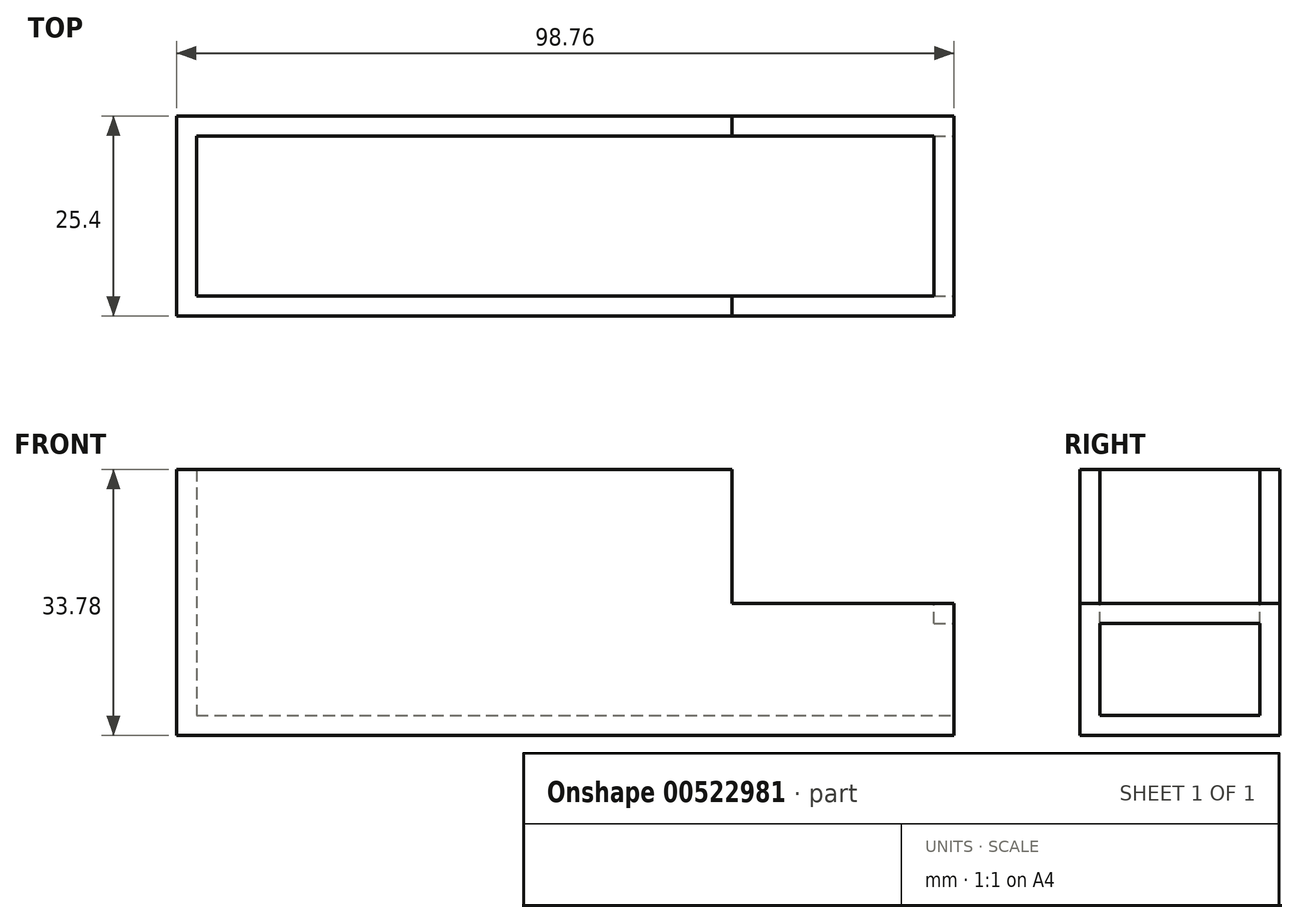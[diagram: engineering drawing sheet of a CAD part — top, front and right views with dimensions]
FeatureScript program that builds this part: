
annotation { "Feature Type Name" : "Feature", "Feature Type Description" : "" }
export const myFeature = defineFeature(function(context is Context, id is Id, definition is map)
    precondition{}
    {
        {
            var Q0;
            Q0=qCreatedBy(makeId("Front.planeOp"),FACE);
            var sketch = newSketch(context, id + "F0", { "sketchPlane" : qUnion([Q0])});
            skLineSegment(sketch, "E0.bottom", {"start": v(-70.56, 33.78) * mm, "end": v(0, 33.78) * mm});
            skLineSegment(sketch, "E0.top", {"start": v(-70.56, 0) * mm, "end": v(0, 0) * mm});
            skLineSegment(sketch, "E0.left", {"start": v(-70.56, 33.78) * mm, "end": v(-70.56, 0) * mm});
            skLineSegment(sketch, "E0.right", {"start": v(0, 33.78) * mm, "end": v(0, 0) * mm});
            skLineSegment(sketch, "E1.bottom", {"start": v(0, 0) * mm, "end": v(28.2, 0) * mm});
            skLineSegment(sketch, "E1.top", {"start": v(0, 16.76) * mm, "end": v(28.2, 16.76) * mm});
            skLineSegment(sketch, "E1.left", {"start": v(0, 0) * mm, "end": v(0, 16.76) * mm});
            skLineSegment(sketch, "E1.right", {"start": v(28.2, 0) * mm, "end": v(28.2, 16.76) * mm});
            skSolve(sketch);
        }
        {
            var Q0;
            Q0 = qSketchRegion(id + "F0", true);
            extrude(context, id + "F1", {"entities" : qUnion([Q0]), "depth" : 25.4 * mm, "offsetDistance" : 25.4 * mm});
        }
        {
            var Q0;
            Q0=makeQuery(id+"F1.opExtrude","SWEPT_FACE",FACE,{"disambiguationData":[OSD([sQuery(id+"F0.wireOp",EDGE,"E0.bottom")])]});
            var sketch = newSketch(context, id + "F2", { "sketchPlane" : qUnion([Q0])});
            skSolve(sketch);
        }
        {
            var Q0;
            Q0=makeQuery(id+"F1.opExtrude","CAP_FACE",FACE,{"disambiguationData":[OSD([sQuery(id+"F0.wireOp",EDGE,"E0.bottom"),sQuery(id+"F0.wireOp",EDGE,"E0.top"),sQuery(id+"F0.wireOp",EDGE,"E0.left"),sQuery(id+"F0.wireOp",EDGE,"E0.right"),sQuery(id+"F0.wireOp",EDGE,"E1.bottom"),sQuery(id+"F0.wireOp",EDGE,"E1.top"),sQuery(id+"F0.wireOp",EDGE,"E1.right")])],"isStart":false});
            var sketch = newSketch(context, id + "F3", { "sketchPlane" : qUnion([Q0])});
            skLineSegment(sketch, "E2.0.0", {"start": v(0, 33.78) * mm, "end": v(-70.56, 33.78) * mm, "construction": true});
            skLineSegment(sketch, "E2.0.2", {"start": v(-70.56, 33.78) * mm, "end": v(0, 33.78) * mm, "construction": true});
            skPoint(sketch, "E2.1", {"position": v(-70.56, 33.78) * mm});
            skSolve(sketch);
        }
        {
            var Q0;
            Q0=makeQuery(id+"F1.opExtrude","SWEPT_FACE",FACE,{"disambiguationData":[OSD([sQuery(id+"F0.wireOp",EDGE,"E0.bottom")])]});
            var Q1;
            Q1=makeQuery(id+"F1.opExtrude","SWEPT_FACE",FACE,{"disambiguationData":[OSD([sQuery(id+"F0.wireOp",EDGE,"E0.right")])]});
            var Q2;
            Q2=makeQuery(id+"F1.opExtrude","SWEPT_FACE",FACE,{"disambiguationData":[OSD([sQuery(id+"F0.wireOp",EDGE,"E1.right")])]});
            shell(context, id + "F4", {"entities" : qUnion([Q0, Q1, Q2]), "thickness" : 2.54 * mm});
        }
        {
            var Q0;
            Q0=makeQuery(id+"F1.opExtrude","SWEPT_FACE",FACE,{"disambiguationData":[OSD([sQuery(id+"F0.wireOp",EDGE,"E1.top")])]});
            var Q1;
            Q1=makeQuery(id+"F1.opExtrude","SWEPT_FACE",FACE,{"disambiguationData":[OSD([sQuery(id+"F0.wireOp",EDGE,"E0.right")])]});
            var Q2;
            Q2=makeQuery(id+"F4.opShell","OFFSET_FACE",FACE,{"disambiguationData":[OSD([sQuery(id+"F0.wireOp",EDGE,"E0.right")]),OD(1.0)]});
            var Q3;
            Q3=makeQuery(id+"F4.opShell","OFFSET_FACE",FACE,{"disambiguationData":[OSD([sQuery(id+"F0.wireOp",EDGE,"E1.top")])]});
            shell(context, id + "F5", {"entities" : qUnion([Q0, Q1, Q2, Q3]), "thickness" : 2.54 * mm});
        }
    });
